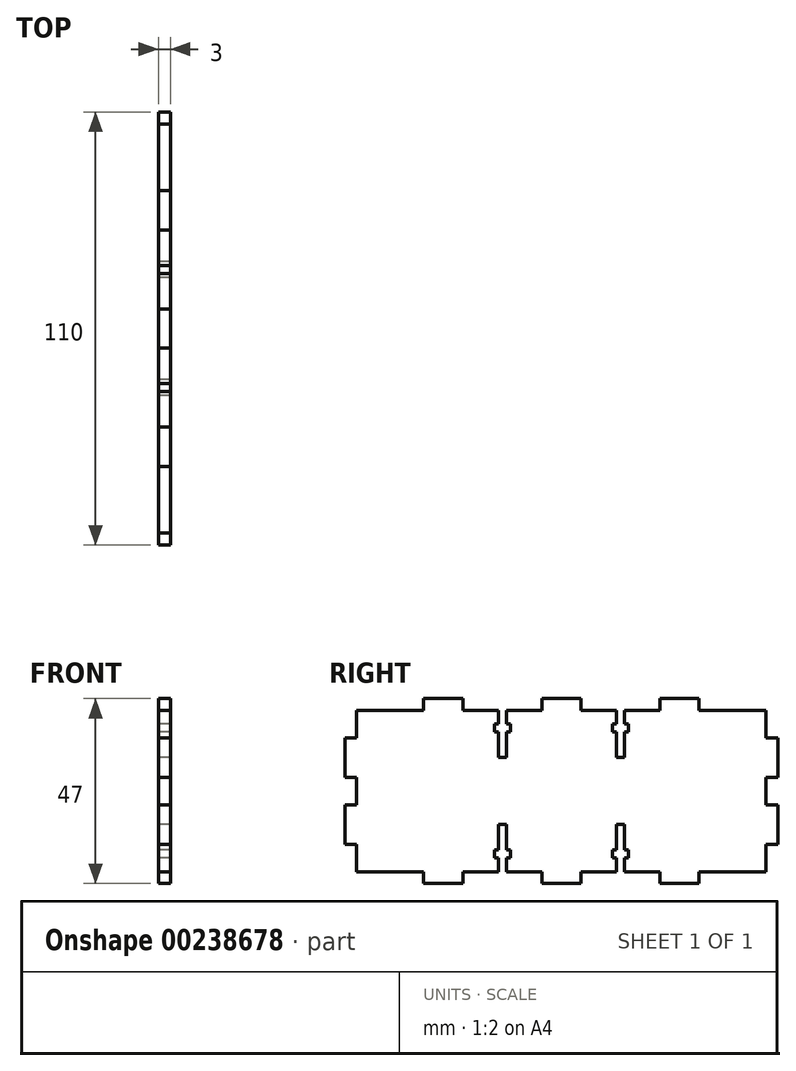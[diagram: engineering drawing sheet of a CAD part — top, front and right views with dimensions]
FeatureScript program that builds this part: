
annotation { "Feature Type Name" : "Feature", "Feature Type Description" : "" }
export const myFeature = defineFeature(function(context is Context, id is Id, definition is map)
    precondition{}
    {
        {
            var Q0;
            Q0=qCreatedBy(makeId("Right.planeOp"),FACE);
            var sketch = newSketch(context, id + "F0", { "sketchPlane" : qUnion([Q0])});
            skLineSegment(sketch, "E0", {"start": v(-52.38, -20.38) * mm, "end": v(-52.38, -13.38) * mm});
            skLineSegment(sketch, "E1", {"start": v(-52.38, -13.38) * mm, "end": v(-55.38, -13.38) * mm});
            skLineSegment(sketch, "E2", {"start": v(-55.38, -13.38) * mm, "end": v(-55.38, -3.38) * mm});
            skLineSegment(sketch, "E3", {"start": v(-55.38, -3.38) * mm, "end": v(-52.38, -3.38) * mm});
            skLineSegment(sketch, "E4", {"start": v(-52.38, -3.38) * mm, "end": v(-52.38, 0.12) * mm});
            skLineSegment(sketch, "E5", {"start": v(-52.38, -20.38) * mm, "end": v(-35.38, -20.38) * mm});
            skLineSegment(sketch, "E6", {"start": v(-35.38, -20.38) * mm, "end": v(-35.38, -23.38) * mm});
            skLineSegment(sketch, "E7", {"start": v(-35.38, -23.38) * mm, "end": v(-25.38, -23.38) * mm});
            skLineSegment(sketch, "E8", {"start": v(-25.38, -20.38) * mm, "end": v(-25.38, -23.38) * mm});
            skLineSegment(sketch, "E9", {"start": v(-25.38, -20.38) * mm, "end": v(-16.38, -20.38) * mm});
            skLineSegment(sketch, "E10", {"start": v(-16.38, -20.38) * mm, "end": v(-16.38, -16.88) * mm});
            skLineSegment(sketch, "E11", {"start": v(-16.38, -16.88) * mm, "end": v(-17.38, -16.88) * mm});
            skLineSegment(sketch, "E12", {"start": v(-17.38, -16.88) * mm, "end": v(-17.38, -14.88) * mm});
            skLineSegment(sketch, "E13", {"start": v(-17.38, -14.88) * mm, "end": v(-16.38, -14.88) * mm});
            skLineSegment(sketch, "E14", {"start": v(-16.38, -14.88) * mm, "end": v(-16.38, -8.38) * mm});
            skLineSegment(sketch, "E15", {"start": v(-16.38, -8.38) * mm, "end": v(-14.38, -8.38) * mm});
            skLineSegment(sketch, "E16", {"start": v(-14.38, -8.38) * mm, "end": v(-14.38, -14.88) * mm});
            skLineSegment(sketch, "E17", {"start": v(-14.38, -14.88) * mm, "end": v(-13.38, -14.88) * mm});
            skLineSegment(sketch, "E18", {"start": v(-14.38, -16.88) * mm, "end": v(-13.38, -16.88) * mm});
            skLineSegment(sketch, "E19", {"start": v(-14.38, -20.38) * mm, "end": v(-14.38, -16.88) * mm});
            skLineSegment(sketch, "E20", {"start": v(-14.38, -20.38) * mm, "end": v(-5.38, -20.38) * mm});
            skLineSegment(sketch, "E21", {"start": v(-13.38, -16.88) * mm, "end": v(-13.38, -14.88) * mm});
            skLineSegment(sketch, "E22", {"start": v(-5.38, -20.38) * mm, "end": v(-5.38, -23.38) * mm});
            skLineSegment(sketch, "E23", {"start": v(-5.38, -23.38) * mm, "end": v(-0.38, -23.38) * mm});
            skLineSegment(sketch, "E24", {"start": v(-52.38, 0.12) * mm, "end": v(-0.38, 0.12) * mm, "construction": true});
            skLineSegment(sketch, "E25", {"start": v(-0.38, 0.12) * mm, "end": v(-0.38, -23.38) * mm, "construction": true});
            skLineSegment(sketch, "E26.MirrorCS", {"start": v(-17.38, 15.12) * mm, "end": v(-16.38, 15.12) * mm});
            skLineSegment(sketch, "E27.MirrorCS", {"start": v(-13.38, 17.12) * mm, "end": v(-13.38, 15.12) * mm});
            skLineSegment(sketch, "E28.MirrorCS", {"start": v(-16.38, 17.12) * mm, "end": v(-17.38, 17.12) * mm});
            skLineSegment(sketch, "E29.MirrorCS", {"start": v(-17.38, 17.12) * mm, "end": v(-17.38, 15.12) * mm});
            skLineSegment(sketch, "E30.MirrorCS", {"start": v(-14.38, 15.12) * mm, "end": v(-13.38, 15.12) * mm});
            skLineSegment(sketch, "E31.MirrorCS", {"start": v(-14.38, 17.12) * mm, "end": v(-13.38, 17.12) * mm});
            skLineSegment(sketch, "E32.MirrorCS", {"start": v(-16.38, 8.62) * mm, "end": v(-14.38, 8.62) * mm});
            skLineSegment(sketch, "E33.MirrorCS", {"start": v(-16.38, 20.62) * mm, "end": v(-16.38, 17.12) * mm});
            skLineSegment(sketch, "E34.MirrorCS", {"start": v(-25.38, 20.62) * mm, "end": v(-25.38, 23.62) * mm});
            skLineSegment(sketch, "E35.MirrorCS", {"start": v(-52.38, 13.62) * mm, "end": v(-55.38, 13.62) * mm});
            skLineSegment(sketch, "E36.MirrorCS", {"start": v(-16.38, 15.12) * mm, "end": v(-16.38, 8.62) * mm});
            skLineSegment(sketch, "E37.MirrorCS", {"start": v(-14.38, 20.62) * mm, "end": v(-14.38, 17.12) * mm});
            skLineSegment(sketch, "E38.MirrorCS", {"start": v(-25.38, 20.62) * mm, "end": v(-16.38, 20.62) * mm});
            skLineSegment(sketch, "E39.MirrorCS", {"start": v(-14.38, 8.62) * mm, "end": v(-14.38, 15.12) * mm});
            skLineSegment(sketch, "E40.MirrorCS", {"start": v(-14.38, 20.62) * mm, "end": v(-5.38, 20.62) * mm});
            skLineSegment(sketch, "E41.MirrorCS", {"start": v(-52.38, 20.62) * mm, "end": v(-35.38, 20.62) * mm});
            skLineSegment(sketch, "E42.MirrorCS", {"start": v(-35.38, 20.62) * mm, "end": v(-35.38, 23.62) * mm});
            skLineSegment(sketch, "E43.MirrorCS", {"start": v(-55.38, 13.62) * mm, "end": v(-55.38, 3.62) * mm});
            skLineSegment(sketch, "E44.MirrorCS", {"start": v(-55.38, 3.62) * mm, "end": v(-52.38, 3.62) * mm});
            skLineSegment(sketch, "E45.MirrorCS", {"start": v(-52.38, 20.62) * mm, "end": v(-52.38, 13.62) * mm});
            skLineSegment(sketch, "E46.MirrorCS", {"start": v(-5.38, 20.62) * mm, "end": v(-5.38, 23.62) * mm});
            skLineSegment(sketch, "E47.MirrorCS", {"start": v(-35.38, 23.62) * mm, "end": v(-25.38, 23.62) * mm});
            skLineSegment(sketch, "E48.MirrorCS", {"start": v(-52.38, 3.62) * mm, "end": v(-52.38, 0.12) * mm});
            skLineSegment(sketch, "E49.MirrorCS", {"start": v(-5.38, 23.62) * mm, "end": v(-0.38, 23.62) * mm});
            skLineSegment(sketch, "E50.MirrorCS", {"start": v(-0.38, 0.12) * mm, "end": v(-0.38, 23.62) * mm, "construction": true});
            skLineSegment(sketch, "E51.MirrorCS", {"start": v(16.62, 17.12) * mm, "end": v(16.62, 15.12) * mm});
            skLineSegment(sketch, "E52.MirrorCS", {"start": v(16.62, 15.12) * mm, "end": v(15.62, 15.12) * mm});
            skLineSegment(sketch, "E53.MirrorCS", {"start": v(15.62, 8.62) * mm, "end": v(13.62, 8.62) * mm});
            skLineSegment(sketch, "E54.MirrorCS", {"start": v(13.62, 17.12) * mm, "end": v(12.62, 17.12) * mm});
            skLineSegment(sketch, "E55.MirrorCS", {"start": v(13.62, -16.88) * mm, "end": v(12.62, -16.88) * mm});
            skLineSegment(sketch, "E56.MirrorCS", {"start": v(15.62, -16.88) * mm, "end": v(16.62, -16.88) * mm});
            skLineSegment(sketch, "E57.MirrorCS", {"start": v(16.62, -16.88) * mm, "end": v(16.62, -14.88) * mm});
            skLineSegment(sketch, "E58.MirrorCS", {"start": v(13.62, -14.88) * mm, "end": v(12.62, -14.88) * mm});
            skLineSegment(sketch, "E59.MirrorCS", {"start": v(12.62, 17.12) * mm, "end": v(12.62, 15.12) * mm});
            skLineSegment(sketch, "E60.MirrorCS", {"start": v(13.62, 15.12) * mm, "end": v(12.62, 15.12) * mm});
            skLineSegment(sketch, "E61.MirrorCS", {"start": v(16.62, -14.88) * mm, "end": v(15.62, -14.88) * mm});
            skLineSegment(sketch, "E62.MirrorCS", {"start": v(12.62, -16.88) * mm, "end": v(12.62, -14.88) * mm});
            skLineSegment(sketch, "E63.MirrorCS", {"start": v(15.62, 17.12) * mm, "end": v(16.62, 17.12) * mm});
            skLineSegment(sketch, "E64.MirrorCS", {"start": v(15.62, -8.38) * mm, "end": v(13.62, -8.38) * mm});
            skLineSegment(sketch, "E65.MirrorCS", {"start": v(24.62, 20.62) * mm, "end": v(24.62, 23.62) * mm});
            skLineSegment(sketch, "E66.MirrorCS", {"start": v(13.62, -20.38) * mm, "end": v(4.62, -20.38) * mm});
            skLineSegment(sketch, "E67.MirrorCS", {"start": v(51.62, 20.62) * mm, "end": v(51.62, 13.62) * mm});
            skLineSegment(sketch, "E68.MirrorCS", {"start": v(34.62, 20.62) * mm, "end": v(34.62, 23.62) * mm});
            skLineSegment(sketch, "E69.MirrorCS", {"start": v(13.62, -20.38) * mm, "end": v(13.62, -16.88) * mm});
            skLineSegment(sketch, "E70.MirrorCS", {"start": v(13.62, -8.38) * mm, "end": v(13.62, -14.88) * mm});
            skLineSegment(sketch, "E71.MirrorCS", {"start": v(15.62, 15.12) * mm, "end": v(15.62, 8.62) * mm});
            skLineSegment(sketch, "E72.MirrorCS", {"start": v(51.62, 3.62) * mm, "end": v(51.62, 0.12) * mm});
            skLineSegment(sketch, "E73.MirrorCS", {"start": v(51.62, 13.62) * mm, "end": v(54.62, 13.62) * mm});
            skLineSegment(sketch, "E74.MirrorCS", {"start": v(34.62, 23.62) * mm, "end": v(24.62, 23.62) * mm});
            skLineSegment(sketch, "E75.MirrorCS", {"start": v(15.62, -20.38) * mm, "end": v(15.62, -16.88) * mm});
            skLineSegment(sketch, "E76.MirrorCS", {"start": v(15.62, 20.62) * mm, "end": v(15.62, 17.12) * mm});
            skLineSegment(sketch, "E77.MirrorCS", {"start": v(34.62, -20.38) * mm, "end": v(34.62, -23.38) * mm});
            skLineSegment(sketch, "E78.MirrorCS", {"start": v(51.62, -20.38) * mm, "end": v(51.62, -13.38) * mm});
            skLineSegment(sketch, "E79.MirrorCS", {"start": v(4.62, 23.62) * mm, "end": v(-0.38, 23.62) * mm});
            skLineSegment(sketch, "E80.MirrorCS", {"start": v(24.62, -20.38) * mm, "end": v(15.62, -20.38) * mm});
            skLineSegment(sketch, "E81.MirrorCS", {"start": v(4.62, -20.38) * mm, "end": v(4.62, -23.38) * mm});
            skLineSegment(sketch, "E82.MirrorCS", {"start": v(51.62, -13.38) * mm, "end": v(54.62, -13.38) * mm});
            skLineSegment(sketch, "E83.MirrorCS", {"start": v(24.62, 20.62) * mm, "end": v(15.62, 20.62) * mm});
            skLineSegment(sketch, "E84.MirrorCS", {"start": v(54.62, 13.62) * mm, "end": v(54.62, 3.62) * mm});
            skLineSegment(sketch, "E85.MirrorCS", {"start": v(54.62, -13.38) * mm, "end": v(54.62, -3.38) * mm});
            skLineSegment(sketch, "E86.MirrorCS", {"start": v(13.62, 8.62) * mm, "end": v(13.62, 15.12) * mm});
            skLineSegment(sketch, "E87.MirrorCS", {"start": v(4.62, -23.38) * mm, "end": v(-0.38, -23.38) * mm});
            skLineSegment(sketch, "E88.MirrorCS", {"start": v(13.62, 20.62) * mm, "end": v(13.62, 17.12) * mm});
            skLineSegment(sketch, "E89.MirrorCS", {"start": v(4.62, 20.62) * mm, "end": v(4.62, 23.62) * mm});
            skLineSegment(sketch, "E90.MirrorCS", {"start": v(13.62, 20.62) * mm, "end": v(4.62, 20.62) * mm});
            skLineSegment(sketch, "E91.MirrorCS", {"start": v(51.62, 0.12) * mm, "end": v(-0.38, 0.12) * mm, "construction": true});
            skLineSegment(sketch, "E92.MirrorCS", {"start": v(54.62, 3.62) * mm, "end": v(51.62, 3.62) * mm});
            skLineSegment(sketch, "E93.MirrorCS", {"start": v(51.62, -20.38) * mm, "end": v(34.62, -20.38) * mm});
            skLineSegment(sketch, "E94.MirrorCS", {"start": v(34.62, -23.38) * mm, "end": v(24.62, -23.38) * mm});
            skLineSegment(sketch, "E95.MirrorCS", {"start": v(15.62, -14.88) * mm, "end": v(15.62, -8.38) * mm});
            skLineSegment(sketch, "E96.MirrorCS", {"start": v(24.62, -20.38) * mm, "end": v(24.62, -23.38) * mm});
            skLineSegment(sketch, "E97.MirrorCS", {"start": v(51.62, 20.62) * mm, "end": v(34.62, 20.62) * mm});
            skLineSegment(sketch, "E98.MirrorCS", {"start": v(51.62, -3.38) * mm, "end": v(51.62, 0.12) * mm});
            skLineSegment(sketch, "E99.MirrorCS", {"start": v(54.62, -3.38) * mm, "end": v(51.62, -3.38) * mm});
            skSolve(sketch);
        }
        {
            var Q0;
            Q0=qSketchRegion(id+"F0",true);
            extrude(context, id + "F1", {"entities" : qUnion([Q0]), "depth" : 3 * mm});
        }
    });
